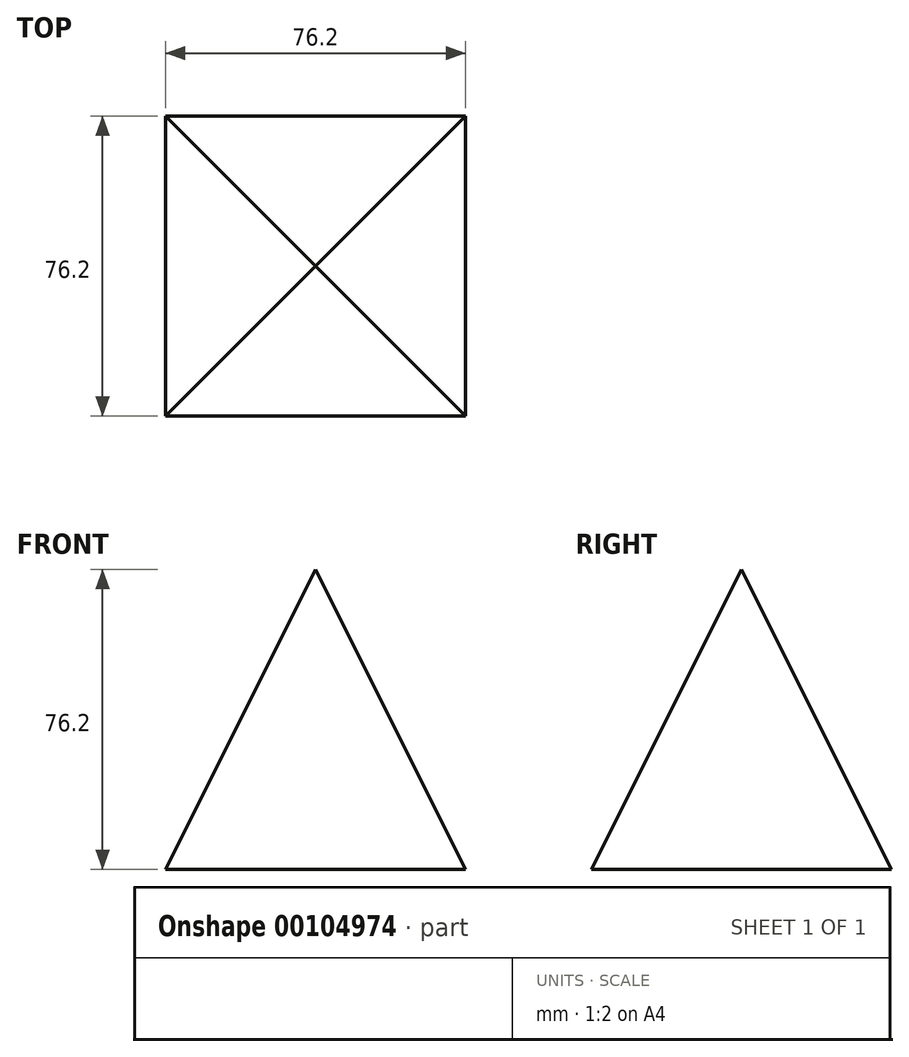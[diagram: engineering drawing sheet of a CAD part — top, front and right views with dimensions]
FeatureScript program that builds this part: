
annotation { "Feature Type Name" : "Feature", "Feature Type Description" : "" }
export const myFeature = defineFeature(function(context is Context, id is Id, definition is map)
    precondition{}
    {
        {
            var Q0;
            Q0=qCreatedBy(makeId("Right.planeOp"),FACE);
            var sketch = newSketch(context, id + "F0", { "sketchPlane" : qUnion([Q0])});
            skLineSegment(sketch, "E0", {"start": v(0, 0) * mm, "end": v(0, 76.2) * mm});
            skLineSegment(sketch, "E1", {"start": v(0, 76.2) * mm, "end": v(-76.2, 76.2) * mm});
            skLineSegment(sketch, "E2", {"start": v(-76.2, 76.2) * mm, "end": v(-76.2, 0) * mm});
            skLineSegment(sketch, "E3", {"start": v(-76.2, 0) * mm, "end": v(0, 0) * mm});
            skSolve(sketch);
        }
        {
            var Q0;
            Q0=makeQuery(id+"F0.imprint","IMPRINT",FACE,{"disambiguationData":[TD([[makeQuery(id+"F0.imprint","IMPRINT",EDGE,{"derivedFrom":sQuery(id+"F0.wireOp",EDGE,"E0")}),1.0]])]});
            extrude(context, id + "F1", {"entities" : qUnion([Q0]), "oppositeDirection" : true, "depth" : 76.2 * mm});
        }
        {
            var Q0;
            Q0=makeQuery(id+"F1.opExtrude","SWEPT_FACE",FACE,{"disambiguationData":[OSD([sQuery(id+"F0.wireOp",EDGE,"E2")])]});
            var sketch = newSketch(context, id + "F2", { "sketchPlane" : qUnion([Q0])});
            skLineSegment(sketch, "E4", {"start": v(-38.1, 76.2) * mm, "end": v(-76.2, 0) * mm});
            skLineSegment(sketch, "E5", {"start": v(-76.2, 0) * mm, "end": v(0, 0) * mm});
            skLineSegment(sketch, "E6", {"start": v(0, 0) * mm, "end": v(-38.1, 76.2) * mm});
            skSolve(sketch);
        }
        {
            var Q0;
            Q0=makeQuery(id+"F1.opExtrude","CAP_FACE",FACE,{"disambiguationData":[OSD([sQuery(id+"F0.wireOp",EDGE,"E0"),sQuery(id+"F0.wireOp",EDGE,"E1"),sQuery(id+"F0.wireOp",EDGE,"E2"),sQuery(id+"F0.wireOp",EDGE,"E3")])],"isStart":false});
            var sketch = newSketch(context, id + "F3", { "sketchPlane" : qUnion([Q0])});
            skLineSegment(sketch, "E7", {"start": v(76.2, 0) * mm, "end": v(0, 0) * mm});
            skLineSegment(sketch, "E8", {"start": v(38.1, 76.2) * mm, "end": v(76.2, 0) * mm});
            skLineSegment(sketch, "E9", {"start": v(0, 0) * mm, "end": v(38.1, 76.2) * mm});
            skSolve(sketch);
        }
        {
            var Q0;
            {var subQ0=sQuery(id+"F3.wireOp",EDGE,"E9");Q0=makeQuery(id+"F3.imprint","IMPRINT",FACE,{"disambiguationData":[TD([[makeQuery(id+"F3.imprint","IMPRINT",EDGE,{"derivedFrom":subQ0}),1.0]])]});}
            var Q1;
            {var subQ0=sQuery(id+"F3.wireOp",EDGE,"E8");Q1=makeQuery(id+"F3.imprint","IMPRINT",FACE,{"disambiguationData":[TD([[makeQuery(id+"F3.imprint","IMPRINT",EDGE,{"derivedFrom":subQ0}),1.0]])]});}
            extrude(context, id + "F4", {"entities" : qUnion([Q0, Q1]), "operationType" : NewBodyOperationType.REMOVE, "oppositeDirection" : true, "depth" : 76.2 * mm});
        }
        {
            var Q0;
            {var subQ0=sQuery(id+"F2.wireOp",EDGE,"E4");Q0=makeQuery(id+"F2.imprint","IMPRINT",FACE,{"disambiguationData":[TD([[makeQuery(id+"F2.imprint","IMPRINT",EDGE,{"derivedFrom":subQ0}),-1.0]])]});}
            var Q1;
            {var subQ0=sQuery(id+"F2.wireOp",EDGE,"E6");Q1=makeQuery(id+"F2.imprint","IMPRINT",FACE,{"disambiguationData":[TD([[makeQuery(id+"F2.imprint","IMPRINT",EDGE,{"derivedFrom":subQ0}),-1.0]])]});}
            extrude(context, id + "F5", {"entities" : qUnion([Q0, Q1]), "operationType" : NewBodyOperationType.REMOVE, "oppositeDirection" : true, "depth" : 76.2 * mm});
        }
    });
